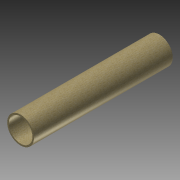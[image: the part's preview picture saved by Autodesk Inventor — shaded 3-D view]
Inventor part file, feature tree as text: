
AUTODESK INVENTOR PART (.ipt)
format: ipt  version: 2012 (Build 160160000, 160)  size: 87,040 bytes
history: native  units: in
note: dims shown in document units (in); Inventor stores cm internally (conversion verified against a paired STEP export)
features: extrude x1, sketch x1
ambient origin geometry x8: Origin, YZ Plane, XZ Plane, XY Plane, X Axis, Y Axis, Z Axis, Center Point
bodies: Solid1 (feature_tree)
feature tree (2):
  extrude  "Extrusion1"  Depth=2.125in
  sketch  "Sketch1"  dims[d0=1.875in d1=2.125in d2=11.0in d3=0.0in]
